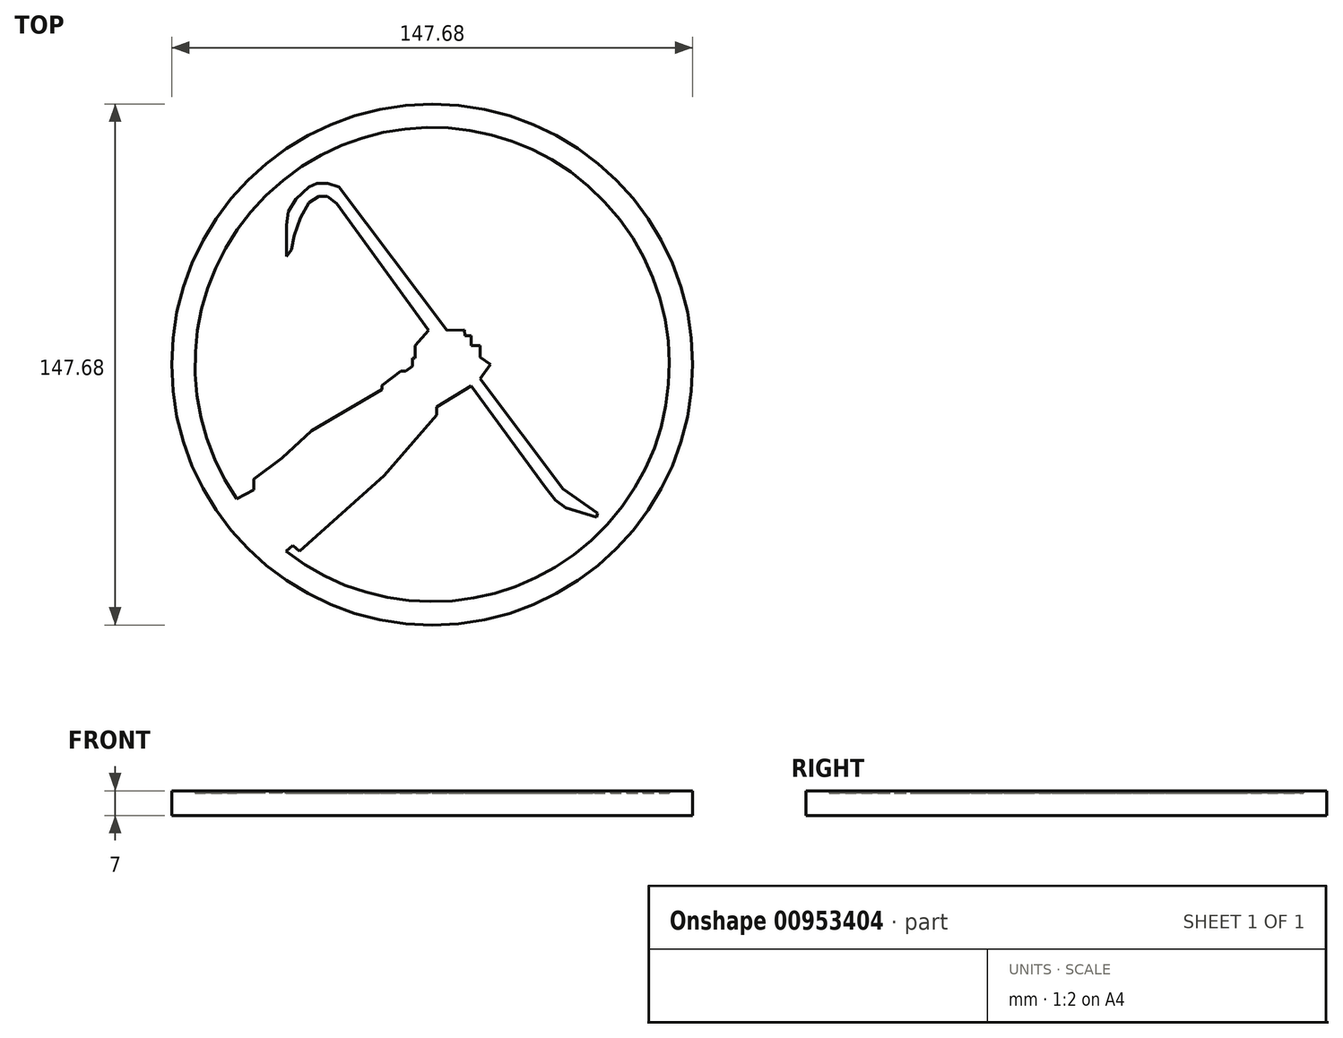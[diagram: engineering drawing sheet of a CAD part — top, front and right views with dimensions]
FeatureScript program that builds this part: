
annotation { "Feature Type Name" : "Feature", "Feature Type Description" : "" }
export const myFeature = defineFeature(function(context is Context, id is Id, definition is map)
    precondition{}
    {
        {
            var Q0;
            Q0=qCreatedBy(makeId("Top.planeOp"),FACE);
            var sketch = newSketch(context, id + "F0", { "sketchPlane" : qUnion([Q0])});
            skCircle(sketch, "E0", {"center": v(0, 0) * mm, "radius": 73.84 * mm});
            skCircle(sketch, "E1", {"center": v(0, 0) * mm, "radius": 67.2 * mm});
            skLineSegment(sketch, "E2", {"start": v(-41.37, -52.97) * mm, "end": v(-39.56, -51.22) * mm});
            skLineSegment(sketch, "E3", {"start": v(-39.56, -51.22) * mm, "end": v(-37.57, -52.87) * mm});
            skLineSegment(sketch, "E4", {"start": v(-37.57, -52.87) * mm, "end": v(-13.6, -31.46) * mm});
            skLineSegment(sketch, "E5", {"start": v(-13.6, -31.46) * mm, "end": v(1.23, -14.35) * mm});
            skLineSegment(sketch, "E6", {"start": v(1.23, -14.35) * mm, "end": v(1.23, -12.08) * mm});
            skLineSegment(sketch, "E7", {"start": v(1.23, -12.08) * mm, "end": v(11.06, -6.04) * mm});
            skLineSegment(sketch, "E8", {"start": v(11.06, -6.04) * mm, "end": v(32.11, -34.93) * mm});
            skLineSegment(sketch, "E9", {"start": v(32.11, -34.93) * mm, "end": v(34.92, -38.4) * mm});
            skLineSegment(sketch, "E10", {"start": v(34.92, -38.4) * mm, "end": v(37.86, -40.55) * mm});
            skLineSegment(sketch, "E11", {"start": v(37.86, -40.55) * mm, "end": v(46.55, -43.22) * mm});
            skLineSegment(sketch, "E12", {"start": v(46.55, -43.22) * mm, "end": v(46.9, -42.09) * mm});
            skLineSegment(sketch, "E13", {"start": v(46.9, -42.09) * mm, "end": v(37.08, -35.3) * mm});
            skLineSegment(sketch, "E14", {"start": v(37.08, -35.3) * mm, "end": v(13.53, -4.03) * mm});
            skLineSegment(sketch, "E15", {"start": v(13.53, -4.03) * mm, "end": v(16.46, 0) * mm});
            skLineSegment(sketch, "E16", {"start": v(16.46, 0) * mm, "end": v(13.53, 2.13) * mm});
            skLineSegment(sketch, "E17", {"start": v(13.53, 2.13) * mm, "end": v(13.53, 5.4) * mm});
            skLineSegment(sketch, "E18", {"start": v(13.53, 5.4) * mm, "end": v(11.06, 5.4) * mm});
            skLineSegment(sketch, "E19", {"start": v(11.06, 5.4) * mm, "end": v(11.06, 8.13) * mm});
            skLineSegment(sketch, "E20", {"start": v(11.06, 8.13) * mm, "end": v(9.25, 8.13) * mm});
            skLineSegment(sketch, "E21", {"start": v(9.25, 8.13) * mm, "end": v(9.19, 9.87) * mm});
            skLineSegment(sketch, "E22", {"start": v(9.19, 9.87) * mm, "end": v(4.17, 9.68) * mm});
            skLineSegment(sketch, "E23", {"start": v(4.17, 9.68) * mm, "end": v(-26.37, 50.37) * mm});
            skLineSegment(sketch, "E24", {"start": v(-26.37, 50.37) * mm, "end": v(-29.58, 51.37) * mm});
            skLineSegment(sketch, "E25", {"start": v(-29.58, 51.37) * mm, "end": v(-32.65, 51.37) * mm});
            skLineSegment(sketch, "E26", {"start": v(-32.65, 51.37) * mm, "end": v(-34.92, 50.37) * mm});
            skLineSegment(sketch, "E27", {"start": v(-34.92, 50.37) * mm, "end": v(-38.67, 46.9) * mm});
            skLineSegment(sketch, "E28", {"start": v(-38.67, 46.9) * mm, "end": v(-40.74, 43.29) * mm});
            skLineSegment(sketch, "E29", {"start": v(-40.74, 43.29) * mm, "end": v(-41.34, 39.48) * mm});
            skLineSegment(sketch, "E30", {"start": v(-41.34, 39.48) * mm, "end": v(-41.34, 30.59) * mm});
            skLineSegment(sketch, "E31", {"start": v(-41.34, 30.59) * mm, "end": v(-39.87, 32.6) * mm});
            skLineSegment(sketch, "E32", {"start": v(-39.87, 32.6) * mm, "end": v(-39.07, 36.54) * mm});
            skLineSegment(sketch, "E33", {"start": v(-39.07, 36.54) * mm, "end": v(-37.4, 41.55) * mm});
            skLineSegment(sketch, "E34", {"start": v(-37.4, 41.55) * mm, "end": v(-34.92, 45.83) * mm});
            skLineSegment(sketch, "E35", {"start": v(-34.92, 45.83) * mm, "end": v(-32.18, 47.7) * mm});
            skLineSegment(sketch, "E36", {"start": v(-32.18, 47.7) * mm, "end": v(-29.78, 47.7) * mm});
            skLineSegment(sketch, "E37", {"start": v(-29.78, 47.7) * mm, "end": v(-27.1, 45.63) * mm});
            skLineSegment(sketch, "E38", {"start": v(-27.1, 45.63) * mm, "end": v(-1.04, 9.68) * mm});
            skLineSegment(sketch, "E39", {"start": v(-1.04, 9.68) * mm, "end": v(-4.85, 5.4) * mm});
            skLineSegment(sketch, "E40", {"start": v(-4.85, 5.4) * mm, "end": v(-4.85, 1.85) * mm});
            skLineSegment(sketch, "E41", {"start": v(-4.85, 1.85) * mm, "end": v(-5.65, 1.85) * mm});
            skLineSegment(sketch, "E42", {"start": v(-5.65, 1.85) * mm, "end": v(-5.65, -0.5) * mm});
            skLineSegment(sketch, "E43", {"start": v(-5.65, -0.5) * mm, "end": v(-7.49, -1.87) * mm});
            skLineSegment(sketch, "E44", {"start": v(-7.49, -1.87) * mm, "end": v(-8.86, -1.87) * mm});
            skLineSegment(sketch, "E45", {"start": v(-8.86, -1.87) * mm, "end": v(-14.18, -5.87) * mm});
            skLineSegment(sketch, "E46", {"start": v(-14.18, -5.87) * mm, "end": v(-14.18, -7.04) * mm});
            skLineSegment(sketch, "E47", {"start": v(-14.18, -7.04) * mm, "end": v(-34.19, -18.8) * mm});
            skLineSegment(sketch, "E48", {"start": v(-34.19, -18.8) * mm, "end": v(-42.61, -26.5) * mm});
            skLineSegment(sketch, "E49", {"start": v(-42.61, -26.5) * mm, "end": v(-50.62, -32.5) * mm});
            skLineSegment(sketch, "E50", {"start": v(-50.62, -32.5) * mm, "end": v(-50.62, -35.51) * mm});
            skLineSegment(sketch, "E51", {"start": v(-50.62, -35.51) * mm, "end": v(-55.35, -38.12) * mm});
            skSolve(sketch);
        }
        {
            var Q0;
            Q0 = qSketchRegion(id + "F0", true);
            var Q1;
            {var subQ0=sQuery(id+"F0.wireOp",EDGE,"E2");Q1=makeQuery(id+"F0.imprint","IMPRINT",FACE,{"disambiguationData":[TD([[makeQuery(id+"F0.imprint","IMPRINT",EDGE,{"derivedFrom":subQ0}),1.0]])]});}
            extrude(context, id + "F1", {"entities" : qUnion([Q0, Q1]), "depth" : 7 * mm, "offsetDistance" : 25 * mm});
        }
        {
            var Q0;
            {var subQ0=sQuery(id+"F0.wireOp",EDGE,"E2");Q0=makeQuery(id+"F0.imprint","IMPRINT",FACE,{"disambiguationData":[TD([[makeQuery(id+"F0.imprint","IMPRINT",EDGE,{"derivedFrom":subQ0}),-1.0]])]});}
            extrude(context, id + "F2", {"entities" : qUnion([Q0]), "operationType" : NewBodyOperationType.ADD, "depth" : 6.3 * mm, "offsetDistance" : 25 * mm});
        }
    });
